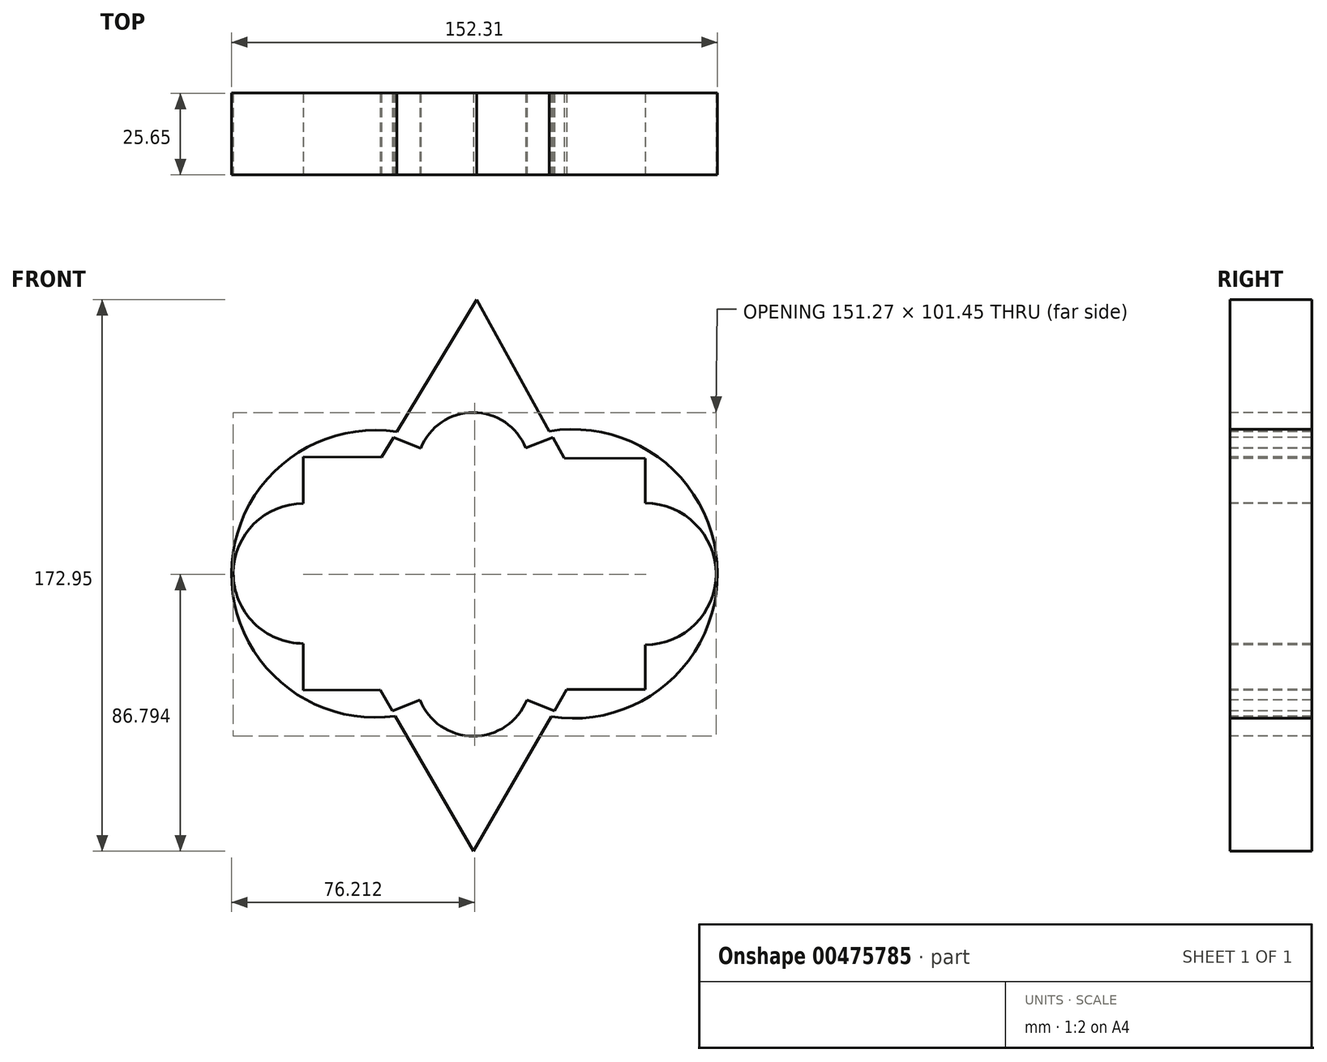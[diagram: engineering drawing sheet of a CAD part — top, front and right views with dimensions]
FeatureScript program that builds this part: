
annotation { "Feature Type Name" : "Feature", "Feature Type Description" : "" }
export const myFeature = defineFeature(function(context is Context, id is Id, definition is map)
    precondition{}
    {
        {
            var Q0;
            Q0=qCreatedBy(makeId("Front.planeOp"),FACE);
            var sketch = newSketch(context, id + "F0", { "sketchPlane" : qUnion([Q0])});
            skLineSegment(sketch, "E0.bottom", {"start": v(-17.15, 14.63) * mm, "end": v(17.15, 14.63) * mm});
            skLineSegment(sketch, "E0.top", {"start": v(-17.15, -14.63) * mm, "end": v(17.15, -14.63) * mm});
            skLineSegment(sketch, "E0.left", {"start": v(-17.15, 14.63) * mm, "end": v(-17.15, -14.63) * mm});
            skLineSegment(sketch, "E0.right", {"start": v(17.15, 14.63) * mm, "end": v(17.15, -14.63) * mm});
            skPoint(sketch, "E0.middle", {"position": v(0, 0) * mm});
            skLineSegment(sketch, "E1", {"start": v(0, 14.63) * mm, "end": v(0, 32.63) * mm});
            skPoint(sketch, "E1.endSnap0", {"position": v(0, 14.63) * mm});
            skLineSegment(sketch, "E2", {"start": v(0, -14.63) * mm, "end": v(0, -33.07) * mm});
            skPoint(sketch, "E2.endSnap0", {"position": v(0, -14.63) * mm});
            skCircle(sketch, "E3", {"center": v(0, 32.63) * mm, "radius": 17.72 * mm});
            skCircle(sketch, "E4", {"center": v(0, -33.07) * mm, "radius": 18.04 * mm});
            skArc(sketch, "E5", {"start": v(0, -33.07) * mm, "mid": v(76.5, -0.22) * mm, "end": v(0, 32.63) * mm});
            skArc(sketch, "E6", {"start": v(0, 32.63) * mm, "mid": v(-75.81, -0.22) * mm, "end": v(0, -33.07) * mm});
            skFitSpline(sketch, "E7", {"points": [v(-30.8, -0.22) * mm, v(-17.15, -14.63) * mm, v(17.15, -14.63) * mm, v(31.2, -0.22) * mm, v(17.15, 14.63) * mm, v(-17.15, 14.63) * mm, v(-30.8, -0.22) * mm]});
            skLineSegment(sketch, "E8", {"start": v(-30.8, -0.22) * mm, "end": v(-30.8, 44.8) * mm});
            skLineSegment(sketch, "E9", {"start": v(-30.8, -0.22) * mm, "end": v(-30.8, -45.24) * mm});
            skLineSegment(sketch, "E10", {"start": v(31.2, -0.22) * mm, "end": v(31.2, 45.08) * mm});
            skLineSegment(sketch, "E11", {"start": v(31.2, -0.22) * mm, "end": v(31.2, -45.52) * mm});
            skLineSegment(sketch, "E12", {"start": v(-17.15, -14.63) * mm, "end": v(-30.8, -45.24) * mm});
            skLineSegment(sketch, "E13", {"start": v(17.15, -14.63) * mm, "end": v(31.2, -45.52) * mm});
            skLineSegment(sketch, "E14", {"start": v(17.15, -14.63) * mm, "end": v(0, -33.07) * mm});
            skLineSegment(sketch, "E15", {"start": v(-17.15, -14.63) * mm, "end": v(0, -33.07) * mm});
            skLineSegment(sketch, "E16", {"start": v(-30.8, -45.24) * mm, "end": v(0, -33.07) * mm});
            skLineSegment(sketch, "E17", {"start": v(31.2, -45.52) * mm, "end": v(0, -33.07) * mm});
            skLineSegment(sketch, "E18", {"start": v(-17.15, 14.63) * mm, "end": v(0, 32.63) * mm});
            skLineSegment(sketch, "E19", {"start": v(-30.8, 44.8) * mm, "end": v(-17.15, 14.63) * mm});
            skLineSegment(sketch, "E20", {"start": v(0, 32.63) * mm, "end": v(17.15, 14.63) * mm});
            skLineSegment(sketch, "E21", {"start": v(31.2, 45.08) * mm, "end": v(17.15, 14.63) * mm});
            skLineSegment(sketch, "E22", {"start": v(0, 32.63) * mm, "end": v(31.2, 45.08) * mm});
            skLineSegment(sketch, "E23", {"start": v(0, 32.63) * mm, "end": v(-30.8, 44.8) * mm});
            skLineSegment(sketch, "E24", {"start": v(-30.8, -0.22) * mm, "end": v(-75.81, 0) * mm});
            skPoint(sketch, "E24.endSnap0", {"position": v(-17.15, 0) * mm});
            skLineSegment(sketch, "E25", {"start": v(-75.81, 0) * mm, "end": v(31.2, -0.22) * mm});
            skLineSegment(sketch, "E26", {"start": v(31.2, -0.22) * mm, "end": v(76.5, -0.31) * mm});
            skCircle(sketch, "E27", {"center": v(-53.3, -0.1) * mm, "radius": 21.93 * mm});
            skCircle(sketch, "E28", {"center": v(53.85, -0.26) * mm, "radius": 22.19 * mm});
            skLineSegment(sketch, "E29.bottom", {"start": v(-67.23, 16.83) * mm, "end": v(-39.38, 16.83) * mm});
            skLineSegment(sketch, "E29.top", {"start": v(-67.23, -17.05) * mm, "end": v(-39.38, -17.05) * mm});
            skLineSegment(sketch, "E29.left", {"start": v(-67.23, 16.83) * mm, "end": v(-67.23, -17.05) * mm});
            skLineSegment(sketch, "E29.right", {"start": v(-39.38, 16.83) * mm, "end": v(-39.38, -17.05) * mm});
            skLineSegment(sketch, "E30.bottom", {"start": v(39.2, 16.4) * mm, "end": v(68.5, 16.4) * mm});
            skLineSegment(sketch, "E30.top", {"start": v(39.2, -16.92) * mm, "end": v(68.5, -16.92) * mm});
            skLineSegment(sketch, "E30.left", {"start": v(39.2, 16.4) * mm, "end": v(39.2, -16.92) * mm});
            skLineSegment(sketch, "E30.right", {"start": v(68.5, 16.4) * mm, "end": v(68.5, -16.92) * mm});
            skArc(sketch, "E31", {"start": v(-67.23, -17.05) * mm, "mid": v(-53.3, -0.1) * mm, "end": v(-67.23, 16.83) * mm});
            skArc(sketch, "E32", {"start": v(-39.38, 16.83) * mm, "mid": v(-53.3, -0.1) * mm, "end": v(-39.38, -17.05) * mm});
            skArc(sketch, "E33", {"start": v(39.2, -16.92) * mm, "mid": v(53.85, -0.26) * mm, "end": v(39.2, 16.4) * mm});
            skArc(sketch, "E34", {"start": v(68.5, 16.4) * mm, "mid": v(53.85, -0.26) * mm, "end": v(68.5, -16.92) * mm});
            skArc(sketch, "E35", {"start": v(-67.23, 16.83) * mm, "mid": v(-38.67, 17.36) * mm, "end": v(-30.8, 44.8) * mm});
            skArc(sketch, "E36", {"start": v(31.2, 45.08) * mm, "mid": v(38.96, 16.57) * mm, "end": v(68.5, 16.4) * mm});
            skArc(sketch, "E37", {"start": v(68.5, -16.92) * mm, "mid": v(39, -17.07) * mm, "end": v(31.2, -45.52) * mm});
            skArc(sketch, "E38", {"start": v(-30.8, -45.24) * mm, "mid": v(-38.57, -17.65) * mm, "end": v(-67.23, -17.05) * mm});
            skLineSegment(sketch, "E39", {"start": v(-53.3, 36.41) * mm, "end": v(-53.3, -36.7) * mm});
            skLineSegment(sketch, "E40", {"start": v(53.85, -36.44) * mm, "end": v(53.85, 35.94) * mm});
            skLineSegment(sketch, "E41", {"start": v(-53.3, 36.41) * mm, "end": v(53.85, 35.94) * mm});
            skLineSegment(sketch, "E42", {"start": v(53.85, -36.44) * mm, "end": v(-53.3, -36.7) * mm});
            skCircle(sketch, "E43.cCircle", {"center": v(0.34, 50.35) * mm, "radius": 17.72 * mm, "construction": true});
            skLineSegment(sketch, "E43.0", {"start": v(30.69, 32.04) * mm, "end": v(-30.69, 33.23) * mm});
            skLineSegment(sketch, "E43.1", {"start": v(-30.69, 33.23) * mm, "end": v(1.03, 85.78) * mm});
            skLineSegment(sketch, "E43.2", {"start": v(1.03, 85.78) * mm, "end": v(30.69, 32.04) * mm});
            skCircle(sketch, "E44.cCircle", {"center": v(0, -51.1) * mm, "radius": 18.04 * mm, "construction": true});
            skLineSegment(sketch, "E44.0", {"start": v(-31.24, -33.07) * mm, "end": v(31.24, -33.07) * mm});
            skLineSegment(sketch, "E44.1", {"start": v(31.24, -33.07) * mm, "end": v(0, -87.17) * mm});
            skLineSegment(sketch, "E44.2", {"start": v(0, -87.17) * mm, "end": v(-31.24, -33.07) * mm});
            skSolve(sketch);
        }
        {
            var Q0;
            {var subQ3=sQuery(id+"F0.wireOp",EDGE,"E3");var subQ6=sQuery(id+"F0.wireOp",EDGE,"E5");var subQ8=makeQuery(id+"F0.imprint","INTERSECT",VERTEX,{"derivedFrom":[subQ3,subQ6]});Q0=makeQuery(id+"F0.imprint","IMPRINT",FACE,{"disambiguationData":[TD([[makeQuery(id+"F0.imprint","IMPRINT",EDGE,{"disambiguationData":[TD([[subQ8,-1.0]])],"derivedFrom":subQ3}),-1.0]])]});}
            extrude(context, id + "F1", {"entities" : qUnion([Q0]), "oppositeDirection" : true, "depth" : 25.4 * mm});
        }
        {
            var Q0;
            Q0 = qSketchRegion(id + "F0", true);
            extrude(context, id + "F2", {"entities" : qUnion([Q0]), "operationType" : NewBodyOperationType.ADD, "oppositeDirection" : true, "depth" : 25.65 * mm});
        }
    });
